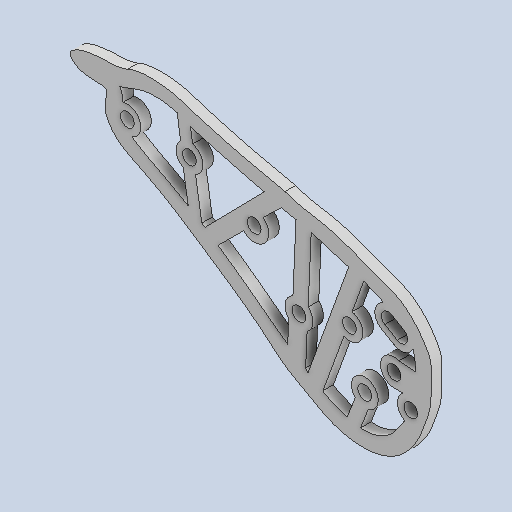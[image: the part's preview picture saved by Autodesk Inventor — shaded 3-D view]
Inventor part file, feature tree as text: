
AUTODESK INVENTOR PART (.ipt)
format: ipt  version: 2022 (Build 260153000, 153)  size: 302,080 bytes
history: native  units: in
note: dims shown in document units (in); Inventor stores cm internally (conversion verified against a paired STEP export)
features: other x3, sketch x1
ambient origin geometry x8: Origin, YZ Plane, XZ Plane, XY Plane, X Axis, Y Axis, Z Axis, Center Point
bodies: Solid1 (feature_tree)
feature tree (4):
  other  "Component26.ipt"
  other  "Solid2::Component26.ipt"
  other  "TaggingFeature1"
  sketch  "Sketch4"  dims[d0=0.3937in]
